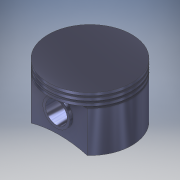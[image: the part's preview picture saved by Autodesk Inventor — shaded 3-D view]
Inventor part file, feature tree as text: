
AUTODESK INVENTOR PART (.ipt)
format: ipt  version: 2019 (Build 230136000, 136)  size: 225,280 bytes
history: native  units: mm
features: extrude x10, sketch x10
ambient origin geometry x8: Origin, YZ Plane, XZ Plane, XY Plane, X Axis, Y Axis, Z Axis, Center Point
bodies: Solid1 (feature_tree)
feature tree (20):
  extrude  "Extrusion1"  Depth=2250.0mm
  extrude  "Extrusion2"  Depth=100.0mm
  extrude  "Extrusion3"  Depth=150.0mm
  extrude  "Extrusion4"  Depth=100.0mm
  extrude  "Extrusion5"  Depth=150.0mm
  extrude  "Extrusion6"  Depth=100.0mm
  extrude  "Extrusion7"  Depth=5800.0mm
  extrude  "Extrusion8"  Depth=1350.0mm
  extrude  "Extrusion9"  Depth=10000.0mm TaperAngle=0.0deg
  extrude  "Extrusion10"  Depth=150.0mm
  sketch  "Sketch1"  dims[d6=2250.0mm d7=0.0mm d8=4250.0mm]
  sketch  "Sketch2"  dims[d9=100.0mm d10=0.0mm d11=4600.0mm]
  sketch  "Sketch3"  dims[d12=150.0mm d13=0.0mm d14=4250.0mm]
  sketch  "Sketch4"  dims[d15=100.0mm d16=0.0mm d17=4600.0mm]
  sketch  "Sketch5"  dims[d18=150.0mm d19=0.0mm d20=4250.0mm]
  sketch  "Sketch6"  dims[d21=100.0mm d22=0.0mm d23=4600.0mm]
  sketch  "Sketch7"  dims[d24=150.0mm d25=0.0mm d26=5800.0mm]
  sketch  "Sketch8"  dims[d27=10000.0mm d28=0.0mm d29=1350.0mm]
  sketch  "Sketch9"  dims[d30=1200.0mm d31=10000.0mm d32=0.0mm]
  sketch  "Sketch10"  dims[d33=1200.0mm d34=1500.0mm d35=150.0mm d36=0.0mm]
